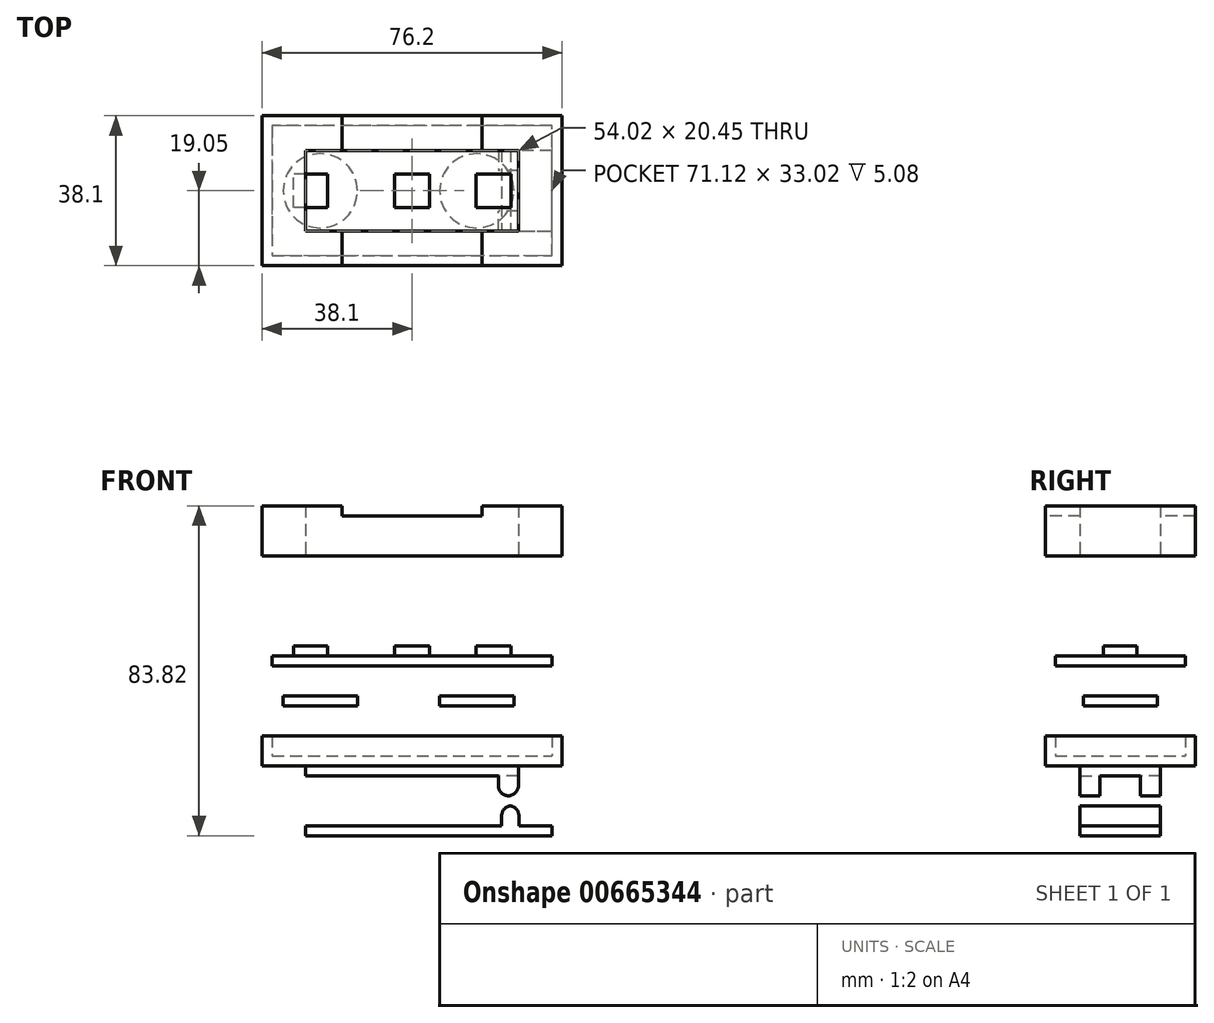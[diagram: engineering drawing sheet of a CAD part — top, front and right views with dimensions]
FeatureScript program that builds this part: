
annotation { "Feature Type Name" : "Feature", "Feature Type Description" : "" }
export const myFeature = defineFeature(function(context is Context, id is Id, definition is map)
    precondition{}
    {
        {
            var Q0;
            Q0=qCreatedBy(makeId("Top.planeOp"),FACE);
            var sketch = newSketch(context, id + "F0", { "sketchPlane" : qUnion([Q0])});
            skLineSegment(sketch, "E0.bottom", {"start": v(38.1, -19.05) * mm, "end": v(-38.1, -19.05) * mm});
            skLineSegment(sketch, "E0.top", {"start": v(38.1, 19.05) * mm, "end": v(-38.1, 19.05) * mm});
            skLineSegment(sketch, "E0.left", {"start": v(38.1, -19.05) * mm, "end": v(38.1, 19.05) * mm});
            skLineSegment(sketch, "E0.right", {"start": v(-38.1, -19.05) * mm, "end": v(-38.1, 19.05) * mm});
            skPoint(sketch, "E0.middle", {"position": v(0, 0) * mm});
            skSolve(sketch);
        }
        {
            var Q0;
            Q0=makeQuery(id+"F0.imprint","IMPRINT",FACE,{"disambiguationData":[TD([[makeQuery(id+"F0.imprint","IMPRINT",EDGE,{"derivedFrom":sQuery(id+"F0.wireOp",EDGE,"E0.bottom")}),-1.0]])]});
            extrude(context, id + "F1", {"entities" : qUnion([Q0]), "depth" : 12.7 * mm, "offsetDistance" : 25.4 * mm});
        }
        {
            var Q0;
            Q0=makeQuery(id+"F1.opExtrude","SWEPT_FACE",FACE,{"disambiguationData":[OSD([sQuery(id+"F0.wireOp",EDGE,"E0.bottom")])]});
            var sketch = newSketch(context, id + "F2", { "sketchPlane" : qUnion([Q0])});
            skLineSegment(sketch, "E1.bottom", {"start": v(17.78, 12.7) * mm, "end": v(-17.78, 12.7) * mm});
            skLineSegment(sketch, "E1.top", {"start": v(17.78, 10.16) * mm, "end": v(-17.78, 10.16) * mm});
            skLineSegment(sketch, "E1.left", {"start": v(17.78, 12.7) * mm, "end": v(17.78, 10.16) * mm});
            skLineSegment(sketch, "E1.right", {"start": v(-17.78, 12.7) * mm, "end": v(-17.78, 10.16) * mm});
            skLineSegment(sketch, "E2", {"start": v(-17.78, 12.7) * mm, "end": v(-38.1, 12.7) * mm, "construction": true});
            skLineSegment(sketch, "E3", {"start": v(17.78, 12.7) * mm, "end": v(38.1, 12.7) * mm, "construction": true});
            skSolve(sketch);
        }
        {
            var Q0;
            Q0=makeQuery(id+"F2.imprint","IMPRINT",FACE,{"disambiguationData":[TD([[makeQuery(id+"F2.imprint","IMPRINT",EDGE,{"derivedFrom":sQuery(id+"F2.wireOp",EDGE,"E1.bottom")}),1.0]])]});
            extrude(context, id + "F3", {"entities" : qUnion([Q0]), "operationType" : NewBodyOperationType.REMOVE, "endBound" : BoundingType.THROUGH_ALL, "oppositeDirection" : true, "depth" : 25.4 * mm, "offsetDistance" : 25.4 * mm});
        }
        {
            var Q0;
            Q0=makeQuery(id+"F1.opExtrude","CAP_FACE",FACE,{"disambiguationData":[OSD([sQuery(id+"F0.wireOp",EDGE,"E0.bottom"),sQuery(id+"F0.wireOp",EDGE,"E0.top"),sQuery(id+"F0.wireOp",EDGE,"E0.left"),sQuery(id+"F0.wireOp",EDGE,"E0.right")])],"isStart":true});
            var sketch = newSketch(context, id + "F4", { "sketchPlane" : qUnion([Q0])});
            skLineSegment(sketch, "E4.bottom", {"start": v(27.01, -10.22) * mm, "end": v(-27.01, -10.22) * mm});
            skLineSegment(sketch, "E4.top", {"start": v(27.01, 10.22) * mm, "end": v(-27.01, 10.22) * mm});
            skLineSegment(sketch, "E4.left", {"start": v(27.01, -10.22) * mm, "end": v(27.01, 10.22) * mm});
            skLineSegment(sketch, "E4.right", {"start": v(-27.01, -10.22) * mm, "end": v(-27.01, 10.22) * mm});
            skPoint(sketch, "E4.middle", {"position": v(0, 0) * mm});
            skSolve(sketch);
        }
        {
            var Q0;
            Q0=makeQuery(id+"F4.imprint","IMPRINT",FACE,{"disambiguationData":[TD([[makeQuery(id+"F4.imprint","IMPRINT",EDGE,{"derivedFrom":sQuery(id+"F4.wireOp",EDGE,"E4.bottom")}),-1.0]])]});
            extrude(context, id + "F5", {"entities" : qUnion([Q0]), "operationType" : NewBodyOperationType.REMOVE, "endBound" : BoundingType.UP_TO_NEXT, "oppositeDirection" : true, "depth" : 25.4 * mm, "offsetDistance" : 25.4 * mm});
        }
        {
            var Q0;
            Q0=makeQuery(id+"F1.opExtrude","CAP_FACE",FACE,{"disambiguationData":[OSD([sQuery(id+"F0.wireOp",EDGE,"E0.bottom"),sQuery(id+"F0.wireOp",EDGE,"E0.top"),sQuery(id+"F0.wireOp",EDGE,"E0.left"),sQuery(id+"F0.wireOp",EDGE,"E0.right")])],"isStart":true});
            cPlane(context, id + "F6", {"entities" : qUnion([Q0]), "cplaneType" : CPlaneType.OFFSET, "offset" : 50.8 * mm, "width" : 152.4 * mm, "height" : 152.4 * mm});
        }
        {
            var Q0;
            Q0=qCreatedBy(id+"F6.planeOp",FACE);
            var sketch = newSketch(context, id + "F7", { "sketchPlane" : qUnion([Q0])});
            skLineSegment(sketch, "E5.0", {"start": v(38.1, 19.05) * mm, "end": v(-38.1, 19.05) * mm});
            skLineSegment(sketch, "E6.0", {"start": v(-38.1, 19.05) * mm, "end": v(-38.1, -19.05) * mm});
            skLineSegment(sketch, "E7.0", {"start": v(38.1, -19.05) * mm, "end": v(-38.1, -19.05) * mm});
            skLineSegment(sketch, "E8.0", {"start": v(38.1, 19.05) * mm, "end": v(38.1, -19.05) * mm});
            skSolve(sketch);
        }
        {
            var Q0;
            Q0=makeQuery(id+"F7.imprint","IMPRINT",FACE,{"disambiguationData":[TD([[makeQuery(id+"F7.imprint","IMPRINT",EDGE,{"derivedFrom":sQuery(id+"F7.wireOp",EDGE,"E5.0")}),1.0]])]});
            extrude(context, id + "F8", {"entities" : qUnion([Q0]), "depth" : 2.54 * mm, "offsetDistance" : 25.4 * mm});
        }
        {
            var Q0;
            Q0=makeQuery(id+"F8.opExtrude","CAP_FACE",FACE,{"disambiguationData":[OSD([sQuery(id+"F7.wireOp",EDGE,"E5.0"),sQuery(id+"F7.wireOp",EDGE,"E6.0"),sQuery(id+"F7.wireOp",EDGE,"E7.0"),sQuery(id+"F7.wireOp",EDGE,"E8.0")])],"isStart":false});
            var sketch = newSketch(context, id + "F9", { "sketchPlane" : qUnion([Q0])});
            skLineSegment(sketch, "E9.0", {"start": v(27.01, 10.22) * mm, "end": v(-27.01, 10.22) * mm});
            skLineSegment(sketch, "E10.0", {"start": v(27.01, -10.22) * mm, "end": v(27.01, 10.22) * mm});
            skLineSegment(sketch, "E11.0", {"start": v(-27.01, -10.22) * mm, "end": v(-27.01, 10.22) * mm});
            skLineSegment(sketch, "E12.0", {"start": v(27.01, -10.22) * mm, "end": v(-27.01, -10.22) * mm});
            skSolve(sketch);
        }
        {
            var Q0;
            Q0=makeQuery(id+"F9.imprint","IMPRINT",FACE,{"disambiguationData":[TD([[makeQuery(id+"F9.imprint","IMPRINT",EDGE,{"derivedFrom":sQuery(id+"F9.wireOp",EDGE,"E9.0")}),1.0]])]});
            extrude(context, id + "F10", {"entities" : qUnion([Q0]), "operationType" : NewBodyOperationType.ADD, "depth" : 2.54 * mm, "offsetDistance" : 25.4 * mm});
        }
        {
            var Q0;
            Q0=makeQuery(id+"F8.opExtrude","CAP_FACE",FACE,{"disambiguationData":[OSD([sQuery(id+"F7.wireOp",EDGE,"E5.0"),sQuery(id+"F7.wireOp",EDGE,"E6.0"),sQuery(id+"F7.wireOp",EDGE,"E7.0"),sQuery(id+"F7.wireOp",EDGE,"E8.0")])],"isStart":true});
            var sketch = newSketch(context, id + "F11", { "sketchPlane" : qUnion([Q0])});
            skLineSegment(sketch, "E13.0", {"start": v(35.56, -16.51) * mm, "end": v(35.56, 16.51) * mm});
            skLineSegment(sketch, "E13.1", {"start": v(-35.56, -16.51) * mm, "end": v(35.56, -16.51) * mm});
            skLineSegment(sketch, "E13.2", {"start": v(-35.56, 16.51) * mm, "end": v(-35.56, -16.51) * mm});
            skLineSegment(sketch, "E13.3", {"start": v(35.56, 16.51) * mm, "end": v(-35.56, 16.51) * mm});
            skSolve(sketch);
        }
        {
            var Q0;
            Q0=makeQuery(id+"F11.imprint","IMPRINT",FACE,{"disambiguationData":[TD([[makeQuery(id+"F11.imprint","IMPRINT",EDGE,{"derivedFrom":sQuery(id+"F11.wireOp",EDGE,"E13.0")}),-1.0]])]});
            extrude(context, id + "F12", {"entities" : qUnion([Q0]), "operationType" : NewBodyOperationType.ADD, "depth" : 5.08 * mm, "offsetDistance" : 25.4 * mm});
        }
        {
            var Q0;
            Q0=makeQuery(id+"F10.opExtrude","CAP_FACE",FACE,{"disambiguationData":[OSD([sQuery(id+"F9.wireOp",EDGE,"E9.0"),sQuery(id+"F9.wireOp",EDGE,"E10.0"),sQuery(id+"F9.wireOp",EDGE,"E11.0"),sQuery(id+"F9.wireOp",EDGE,"E12.0")])],"isStart":false});
            var sketch = newSketch(context, id + "F13", { "sketchPlane" : qUnion([Q0])});
            skLineSegment(sketch, "E14.bottom", {"start": v(27.01, 10.22) * mm, "end": v(21.93, 10.22) * mm});
            skLineSegment(sketch, "E14.top", {"start": v(27.01, 5.14) * mm, "end": v(21.93, 5.14) * mm});
            skLineSegment(sketch, "E14.left", {"start": v(27.01, 10.22) * mm, "end": v(27.01, 5.14) * mm});
            skLineSegment(sketch, "E14.right", {"start": v(21.93, 10.22) * mm, "end": v(21.93, 5.14) * mm});
            skLineSegment(sketch, "E15.bottom", {"start": v(27.01, -10.22) * mm, "end": v(21.93, -10.22) * mm});
            skLineSegment(sketch, "E15.top", {"start": v(27.01, -5.14) * mm, "end": v(21.93, -5.14) * mm});
            skLineSegment(sketch, "E15.left", {"start": v(27.01, -10.22) * mm, "end": v(27.01, -5.14) * mm});
            skLineSegment(sketch, "E15.right", {"start": v(21.93, -10.22) * mm, "end": v(21.93, -5.14) * mm});
            skSolve(sketch);
        }
        {
            var Q0;
            Q0=makeQuery(id+"F13.imprint","IMPRINT",FACE,{"disambiguationData":[TD([[makeQuery(id+"F13.imprint","IMPRINT",EDGE,{"derivedFrom":sQuery(id+"F13.wireOp",EDGE,"E14.bottom")}),1.0]])]});
            var Q1;
            Q1=makeQuery(id+"F13.imprint","IMPRINT",FACE,{"disambiguationData":[TD([[makeQuery(id+"F13.imprint","IMPRINT",EDGE,{"derivedFrom":sQuery(id+"F13.wireOp",EDGE,"E15.bottom")}),-1.0]])]});
            extrude(context, id + "F14", {"entities" : qUnion([Q0, Q1]), "operationType" : NewBodyOperationType.ADD, "depth" : 5.08 * mm, "offsetDistance" : 25.4 * mm});
        }
        {
            var Q0;
            Q0=makeQuery(id+"F14.opExtrude","CAP_EDGE",EDGE,{"disambiguationData":[OSD([sQuery(id+"F13.wireOp",EDGE,"E14.right")])],"isStart":false});
            var Q1;
            Q1=makeQuery(id+"F14.opExtrude","CAP_EDGE",EDGE,{"disambiguationData":[OSD([sQuery(id+"F13.wireOp",EDGE,"E14.left")])],"isStart":false});
            var Q2;
            Q2=makeQuery(id+"F14.opExtrude","CAP_EDGE",EDGE,{"disambiguationData":[OSD([sQuery(id+"F13.wireOp",EDGE,"E15.left")])],"isStart":false});
            var Q3;
            Q3=makeQuery(id+"F14.opExtrude","CAP_EDGE",EDGE,{"disambiguationData":[OSD([sQuery(id+"F13.wireOp",EDGE,"E15.right")])],"isStart":false});
            fillet(context, id + "F15", {"entities" : qUnion([Q0, Q1, Q2, Q3]), "radius" : 2.54 * mm, "tangentPropagation" : true, "allowEdgeOverflow" : false});
        }
        {
            var Q0;
            Q0=makeQuery(id+"F10.opExtrude","CAP_FACE",FACE,{"disambiguationData":[OSD([sQuery(id+"F9.wireOp",EDGE,"E9.0"),sQuery(id+"F9.wireOp",EDGE,"E10.0"),sQuery(id+"F9.wireOp",EDGE,"E11.0"),sQuery(id+"F9.wireOp",EDGE,"E12.0")])],"isStart":false});
            cPlane(context, id + "F16", {"entities" : qUnion([Q0]), "cplaneType" : CPlaneType.OFFSET, "offset" : 12.7 * mm, "width" : 152.4 * mm, "height" : 152.4 * mm});
        }
        {
            var Q0;
            Q0=qCreatedBy(id+"F16.planeOp",FACE);
            var sketch = newSketch(context, id + "F17", { "sketchPlane" : qUnion([Q0])});
            skLineSegment(sketch, "E16.0", {"start": v(-27.01, -10.22) * mm, "end": v(-27.01, 10.22) * mm});
            skLineSegment(sketch, "E17.0", {"start": v(21.93, 10.22) * mm, "end": v(-27.01, 10.22) * mm});
            skLineSegment(sketch, "E18.0", {"start": v(21.93, -10.22) * mm, "end": v(-27.01, -10.22) * mm});
            skLineSegment(sketch, "E19", {"start": v(21.93, 10.22) * mm, "end": v(35.5, 10.22) * mm});
            skLineSegment(sketch, "E20", {"start": v(35.5, 10.22) * mm, "end": v(35.5, -10.22) * mm});
            skLineSegment(sketch, "E21", {"start": v(35.5, -10.22) * mm, "end": v(21.93, -10.22) * mm});
            skSolve(sketch);
        }
        {
            var Q0;
            Q0=makeQuery(id+"F17.imprint","IMPRINT",FACE,{"disambiguationData":[TD([[makeQuery(id+"F17.imprint","IMPRINT",EDGE,{"derivedFrom":sQuery(id+"F17.wireOp",EDGE,"E16.0")}),-1.0]])]});
            extrude(context, id + "F18", {"entities" : qUnion([Q0]), "depth" : 2.54 * mm, "offsetDistance" : 25.4 * mm});
        }
        {
            var Q0;
            Q0=makeQuery(id+"F1.opExtrude","CAP_FACE",FACE,{"disambiguationData":[OSD([sQuery(id+"F0.wireOp",EDGE,"E0.bottom"),sQuery(id+"F0.wireOp",EDGE,"E0.top"),sQuery(id+"F0.wireOp",EDGE,"E0.left"),sQuery(id+"F0.wireOp",EDGE,"E0.right")])],"isStart":true});
            cPlane(context, id + "F19", {"entities" : qUnion([Q0]), "cplaneType" : CPlaneType.OFFSET, "offset" : 25.4 * mm, "width" : 152.4 * mm, "height" : 152.4 * mm});
        }
        {
            var Q0;
            Q0=qCreatedBy(id+"F19.planeOp",FACE);
            var sketch = newSketch(context, id + "F20", { "sketchPlane" : qUnion([Q0])});
            skLineSegment(sketch, "E22.0.0", {"start": v(35.56, 16.51) * mm, "end": v(35.56, -16.51) * mm});
            skLineSegment(sketch, "E22.0.1", {"start": v(35.56, -16.51) * mm, "end": v(-35.56, -16.51) * mm});
            skLineSegment(sketch, "E22.0.2", {"start": v(-35.56, -16.51) * mm, "end": v(-35.56, 16.51) * mm});
            skLineSegment(sketch, "E22.0.3", {"start": v(-35.56, 16.51) * mm, "end": v(35.56, 16.51) * mm});
            skSolve(sketch);
        }
        {
            var Q0;
            Q0=makeQuery(id+"F20.imprint","IMPRINT",FACE,{"disambiguationData":[TD([[makeQuery(id+"F20.imprint","IMPRINT",EDGE,{"derivedFrom":sQuery(id+"F20.wireOp",EDGE,"E22.0.0")}),-1.0]])]});
            extrude(context, id + "F21", {"entities" : qUnion([Q0]), "depth" : 2.54 * mm, "offsetDistance" : 25.4 * mm});
        }
        {
            var Q0;
            Q0=makeQuery(id+"F21.opExtrude","CAP_FACE",FACE,{"disambiguationData":[OSD([sQuery(id+"F20.wireOp",EDGE,"E22.0.0"),sQuery(id+"F20.wireOp",EDGE,"E22.0.1"),sQuery(id+"F20.wireOp",EDGE,"E22.0.2"),sQuery(id+"F20.wireOp",EDGE,"E22.0.3")])],"isStart":true});
            var sketch = newSketch(context, id + "F22", { "sketchPlane" : qUnion([Q0])});
            skLineSegment(sketch, "E23.bottom", {"start": v(4.42, -4.27) * mm, "end": v(-4.42, -4.27) * mm});
            skLineSegment(sketch, "E23.top", {"start": v(4.42, 4.27) * mm, "end": v(-4.42, 4.27) * mm});
            skLineSegment(sketch, "E23.left", {"start": v(4.42, -4.27) * mm, "end": v(4.42, 4.27) * mm});
            skLineSegment(sketch, "E23.right", {"start": v(-4.42, -4.27) * mm, "end": v(-4.42, 4.27) * mm});
            skPoint(sketch, "E23.middle", {"position": v(0, 0) * mm});
            skLineSegment(sketch, "E24.bottom", {"start": v(-21.5, -4.27) * mm, "end": v(-30.04, -4.27) * mm});
            skLineSegment(sketch, "E24.top", {"start": v(-21.5, 4.27) * mm, "end": v(-30.04, 4.27) * mm});
            skLineSegment(sketch, "E24.left", {"start": v(-21.5, -4.27) * mm, "end": v(-21.5, 4.27) * mm});
            skLineSegment(sketch, "E24.right", {"start": v(-30.04, -4.27) * mm, "end": v(-30.04, 4.27) * mm});
            skPoint(sketch, "E24.middle", {"position": v(-25.77, 0) * mm});
            skLineSegment(sketch, "E25.bottom", {"start": v(25.13, -4.27) * mm, "end": v(16.28, -4.27) * mm});
            skLineSegment(sketch, "E25.top", {"start": v(25.13, 4.27) * mm, "end": v(16.28, 4.27) * mm});
            skLineSegment(sketch, "E25.left", {"start": v(25.13, -4.27) * mm, "end": v(25.13, 4.27) * mm});
            skLineSegment(sketch, "E25.right", {"start": v(16.28, -4.27) * mm, "end": v(16.28, 4.27) * mm});
            skPoint(sketch, "E25.middle", {"position": v(20.7, 0) * mm});
            skSolve(sketch);
        }
        {
            var Q0;
            Q0=makeQuery(id+"F22.imprint","IMPRINT",FACE,{"disambiguationData":[TD([[makeQuery(id+"F22.imprint","IMPRINT",EDGE,{"derivedFrom":sQuery(id+"F22.wireOp",EDGE,"E24.bottom")}),-1.0]])]});
            var Q1;
            Q1=makeQuery(id+"F22.imprint","IMPRINT",FACE,{"disambiguationData":[TD([[makeQuery(id+"F22.imprint","IMPRINT",EDGE,{"derivedFrom":sQuery(id+"F22.wireOp",EDGE,"E23.bottom")}),-1.0]])]});
            var Q2;
            Q2=makeQuery(id+"F22.imprint","IMPRINT",FACE,{"disambiguationData":[TD([[makeQuery(id+"F22.imprint","IMPRINT",EDGE,{"derivedFrom":sQuery(id+"F22.wireOp",EDGE,"E25.bottom")}),-1.0]])]});
            extrude(context, id + "F23", {"entities" : qUnion([Q0, Q1, Q2]), "operationType" : NewBodyOperationType.ADD, "depth" : 2.54 * mm, "offsetDistance" : 25.4 * mm});
        }
        {
            var Q0;
            Q0=makeQuery(id+"F21.opExtrude","CAP_FACE",FACE,{"disambiguationData":[OSD([sQuery(id+"F20.wireOp",EDGE,"E22.0.0"),sQuery(id+"F20.wireOp",EDGE,"E22.0.1"),sQuery(id+"F20.wireOp",EDGE,"E22.0.2"),sQuery(id+"F20.wireOp",EDGE,"E22.0.3")])],"isStart":false});
            cPlane(context, id + "F24", {"entities" : qUnion([Q0]), "cplaneType" : CPlaneType.OFFSET, "offset" : 7.62 * mm, "width" : 152.4 * mm, "height" : 152.4 * mm});
        }
        {
            var Q0;
            Q0=qCreatedBy(id+"F24.planeOp",FACE);
            var sketch = newSketch(context, id + "F25", { "sketchPlane" : qUnion([Q0])});
            skLineSegment(sketch, "E26.0.0", {"start": v(35.56, 16.51) * mm, "end": v(-35.56, 16.51) * mm, "construction": true});
            skLineSegment(sketch, "E26.0.1", {"start": v(-35.56, 16.51) * mm, "end": v(-35.56, -16.51) * mm, "construction": true});
            skLineSegment(sketch, "E26.0.2", {"start": v(-35.56, -16.51) * mm, "end": v(35.56, -16.51) * mm, "construction": true});
            skLineSegment(sketch, "E26.0.3", {"start": v(35.56, -16.51) * mm, "end": v(35.56, 16.51) * mm, "construction": true});
            skLineSegment(sketch, "E27", {"start": v(-35.56, 0) * mm, "end": v(35.56, 0) * mm, "construction": true});
            skCircle(sketch, "E28", {"center": v(-23.3, 0) * mm, "radius": 9.42 * mm});
            skCircle(sketch, "E29", {"center": v(16.44, 0) * mm, "radius": 9.42 * mm});
            skSolve(sketch);
        }
        {
            var Q0;
            Q0=makeQuery(id+"F25.imprint","IMPRINT",FACE,{"disambiguationData":[TD([[makeQuery(id+"F25.imprint","IMPRINT",EDGE,{"derivedFrom":sQuery(id+"F25.wireOp",EDGE,"E28")}),1.0]])]});
            var Q1;
            Q1=makeQuery(id+"F25.imprint","IMPRINT",FACE,{"disambiguationData":[TD([[makeQuery(id+"F25.imprint","IMPRINT",EDGE,{"derivedFrom":sQuery(id+"F25.wireOp",EDGE,"E29")}),1.0]])]});
            extrude(context, id + "F26", {"entities" : qUnion([Q0, Q1]), "depth" : 2.54 * mm, "offsetDistance" : 25.4 * mm});
        }
        {
            var Q0;
            Q0=makeQuery(id+"F18.opExtrude","CAP_FACE",FACE,{"disambiguationData":[OSD([sQuery(id+"F17.wireOp",EDGE,"E16.0"),sQuery(id+"F17.wireOp",EDGE,"E17.0"),sQuery(id+"F17.wireOp",EDGE,"E18.0"),sQuery(id+"F17.wireOp",EDGE,"E19"),sQuery(id+"F17.wireOp",EDGE,"E20"),sQuery(id+"F17.wireOp",EDGE,"E21")])],"isStart":true});
            var sketch = newSketch(context, id + "F27", { "sketchPlane" : qUnion([Q0])});
            skLineSegment(sketch, "E30.bottom", {"start": v(27.14, 10.22) * mm, "end": v(22.8, 10.22) * mm});
            skLineSegment(sketch, "E30.top", {"start": v(27.14, -10.22) * mm, "end": v(22.8, -10.22) * mm});
            skLineSegment(sketch, "E30.left", {"start": v(27.14, 10.22) * mm, "end": v(27.14, -10.22) * mm});
            skLineSegment(sketch, "E30.right", {"start": v(22.8, 10.22) * mm, "end": v(22.8, -10.22) * mm});
            skSolve(sketch);
        }
        {
            var Q0;
            Q0=makeQuery(id+"F27.imprint","IMPRINT",FACE,{"disambiguationData":[TD([[makeQuery(id+"F27.imprint","IMPRINT",EDGE,{"derivedFrom":sQuery(id+"F27.wireOp",EDGE,"E30.bottom")}),1.0]])]});
            extrude(context, id + "F28", {"entities" : qUnion([Q0]), "operationType" : NewBodyOperationType.ADD, "depth" : 5.08 * mm, "offsetDistance" : 25.4 * mm});
        }
        {
            var Q0;
            Q0=makeQuery(id+"F28.opExtrude","CAP_EDGE",EDGE,{"disambiguationData":[OSD([sQuery(id+"F27.wireOp",EDGE,"E30.left")])],"isStart":false});
            var Q1;
            Q1=makeQuery(id+"F28.opExtrude","CAP_EDGE",EDGE,{"disambiguationData":[OSD([sQuery(id+"F27.wireOp",EDGE,"E30.right")])],"isStart":false});
            fillet(context, id + "F29", {"entities" : qUnion([Q0, Q1]), "radius" : 2.54 * mm, "tangentPropagation" : true, "allowEdgeOverflow" : false});
        }
    });
